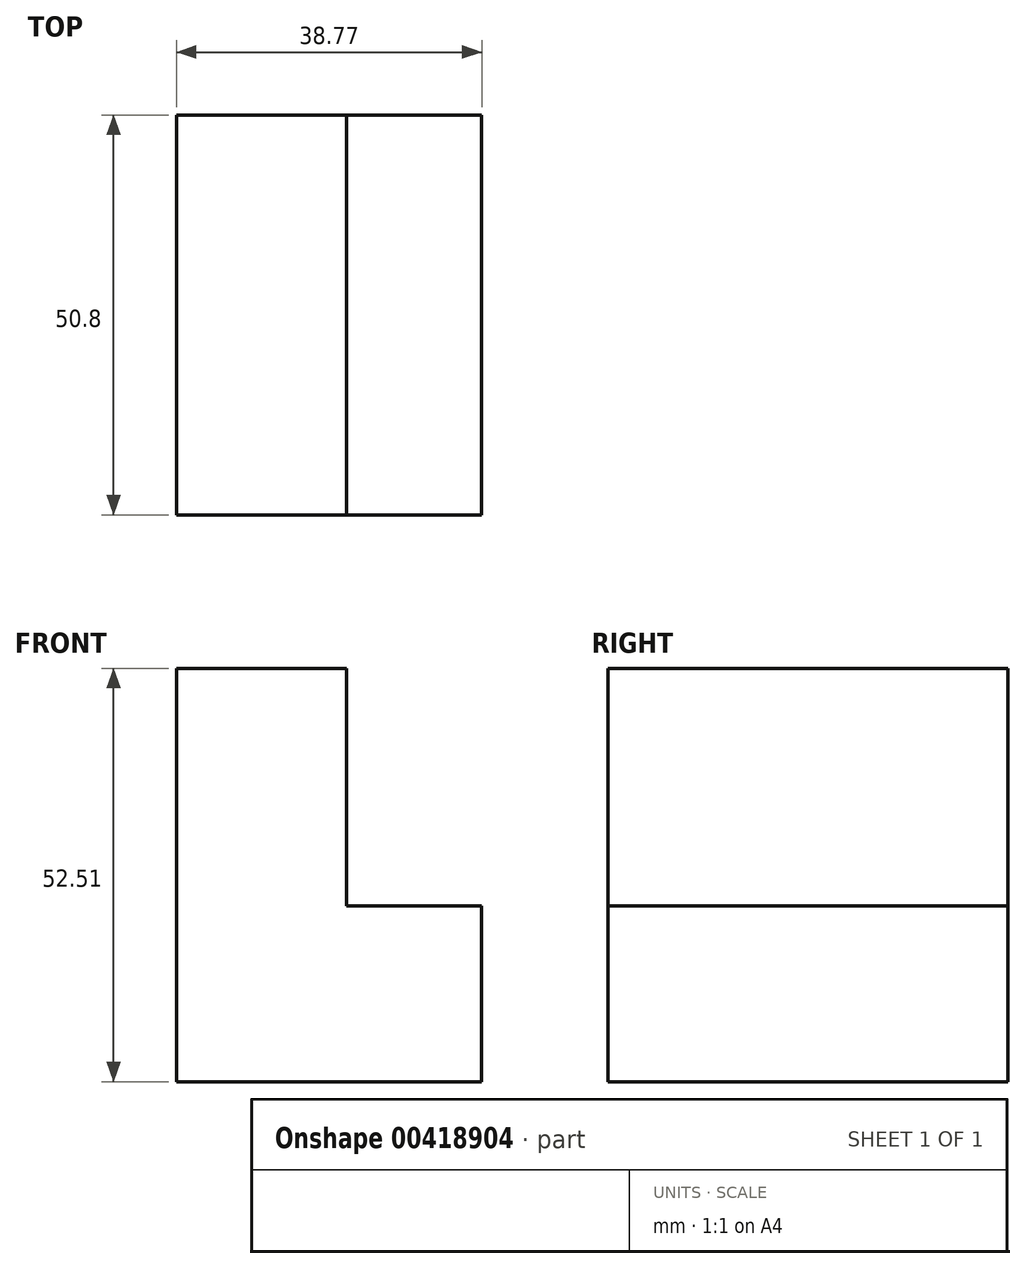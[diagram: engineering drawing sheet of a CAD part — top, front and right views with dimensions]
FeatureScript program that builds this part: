
annotation { "Feature Type Name" : "Feature", "Feature Type Description" : "" }
export const myFeature = defineFeature(function(context is Context, id is Id, definition is map)
    precondition{}
    {
        {
            var Q0;
            Q0=qCreatedBy(makeId("Front.planeOp"),FACE);
            var sketch = newSketch(context, id + "F0", { "sketchPlane" : qUnion([Q0])});
            skLineSegment(sketch, "E0", {"start": v(-8.02, 3.63) * mm, "end": v(-47.74, 3.63) * mm});
            skLineSegment(sketch, "E1", {"start": v(-47.74, 3.63) * mm, "end": v(-47.74, 37.8) * mm});
            skLineSegment(sketch, "E2", {"start": v(-47.74, 37.8) * mm, "end": v(-47.74, 56.14) * mm});
            skLineSegment(sketch, "E3", {"start": v(-47.74, 56.14) * mm, "end": v(-26.16, 56.14) * mm});
            skLineSegment(sketch, "E4", {"start": v(-26.16, 56.14) * mm, "end": v(-26.16, 25.97) * mm});
            skLineSegment(sketch, "E5", {"start": v(-26.16, 25.97) * mm, "end": v(-8.97, 25.97) * mm});
            skLineSegment(sketch, "E6", {"start": v(-8.97, 25.97) * mm, "end": v(-8.97, 3.63) * mm});
            skSolve(sketch);
        }
        {
            var Q0;
            {var subQ0=sQuery(id+"F0.wireOp",EDGE,"E1");Q0=makeQuery(id+"F0.imprint","IMPRINT",FACE,{"disambiguationData":[TD([[makeQuery(id+"F0.imprint","IMPRINT",EDGE,{"derivedFrom":subQ0}),-1.0]])]});}
            extrude(context, id + "F1", {"entities" : qUnion([Q0]), "depth" : 50.8 * mm});
        }
    });
